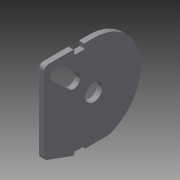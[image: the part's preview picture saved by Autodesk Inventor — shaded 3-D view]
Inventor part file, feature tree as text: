
AUTODESK INVENTOR PART (.ipt)
format: ipt  version: 2015 (Build 190159000, 159)  size: 143,360 bytes
history: native  units: mm
features: fillet x2, extrude x1, sketch x1
ambient origin geometry x8: Origin, YZ Plane, XZ Plane, XY Plane, X Axis, Y Axis, Z Axis, Center Point
bodies: Body1 (feature_tree)
feature tree (4):
  extrude  "Extrusion4"  Depth=1.5mm
  fillet  "Fillet1"  Radius=15.0mm
  fillet  "Fillet2"  Radius=15.0mm
  sketch  "Sketch1"  dims[d3=32.5mm d4=94.0mm d6=15.0mm d7=15.0mm d9=20.0mm d13=52.0mm d18=55.0mm d20=100.0mm d31=55.0mm d34=58.0mm d52=5.0mm d54=47.0mm d56=1.0mm d59=20.0mm d60=12.0mm d61=6.0mm d65=0.5mm d69=60.0mm d70=6.0mm d71=0.0mm d72=95.0mm d73=5.0mm d74=19.198622mm d75=3.0mm d76=12.0mm d77=35.0mm d78=1.5mm]
